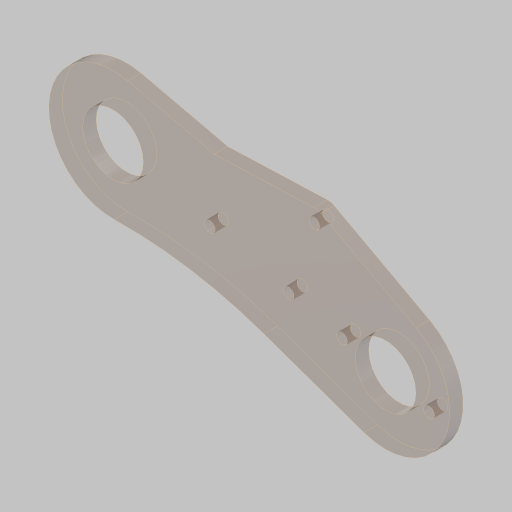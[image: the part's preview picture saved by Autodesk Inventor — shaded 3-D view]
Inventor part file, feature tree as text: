
AUTODESK INVENTOR PART (.ipt)
format: ipt  version: 2023.5 (Build 275446000, 446)  size: 241,664 bytes
history: native  units: in
note: dims shown in document units (in); Inventor stores cm internally (conversion verified against a paired STEP export)
features: sketch x4, hole x3, extrude x2, projected_geometry x2
ambient origin geometry x8: Origin, YZ Plane, XZ Plane, XY Plane, X Axis, Y Axis, Z Axis, Center Point
bodies: Solid1 (feature_tree)
feature tree (11):
  sketch  "Sketch1"  dims[d3=45.0deg d4=0.0in]
  extrude  "Extrusion1"  TaperAngle=0.0deg  [1 undecoded]
  hole  "Hole1"  [1 undecoded]
  hole  "Hole2"  [1 undecoded]
  extrude  "Extrusion2"  Depth=0.25in
  hole  "Hole3"  [1 undecoded]
  sketch  "Sketch2"  dims[d7=4.0in d8=4.0in]
  projected_geometry  "Projected Loop1"
  sketch  "Sketch3"  dims[d9=1.123in d10=4.0in]
  projected_geometry  "Projected Loop2"
  sketch  "Sketch4"  dims[d11=4.5in d12=4.5in d13=0.625in d14=0.625in d15=5.181in d16=1.128in d17=5.181in d18=1.8765in d19=1.8765in d22=1.0in d23=6.0in d26=10.5532in d27=2.5in d30=8.0in d31=0.0687in d33=4.75in d34=1.375in d35=0.75in d36=0.25in d38=2.3622in d40=360.0deg d44=0.375in d45=0.25in d46=0.0in d47=0.201in d48=0.75in d49=0.37in d50=0.25in d51=90.0deg d52=1.0in d53=0.8108in d55=0.5497in d56=0.3in d57=0.25in d58=2.256in d59=2.5in d60=2.9555in d61=2.35in d62=0.3779in d65=2.0in d66=2.3622in d68=360.0deg d70=1.625in d71=60.0deg d73=0.201in d74=0.75in d75=0.385in d76=0.25in d77=0.5635in d78=1.0in d79=0.8108in d80=1.5748in d82=360.0deg d85=1.5748in d87=360.0deg d89=45.0deg d90=1.6875in d91=1.43in d92=0.5in d93=0.25in d94=0.0in d95=0.201in d96=0.75in d97=0.385in d98=0.25in d99=0.5635in d100=1.0in d101=0.8108in d102=0.25in d103=0.1045in d104=0.1045in d105=1.5in]
note: 4 required parameter values undecoded (feature->parameter linkage not recoverable at this tier; creation-order binding heuristic only, values carry confidence <= 0.55)
